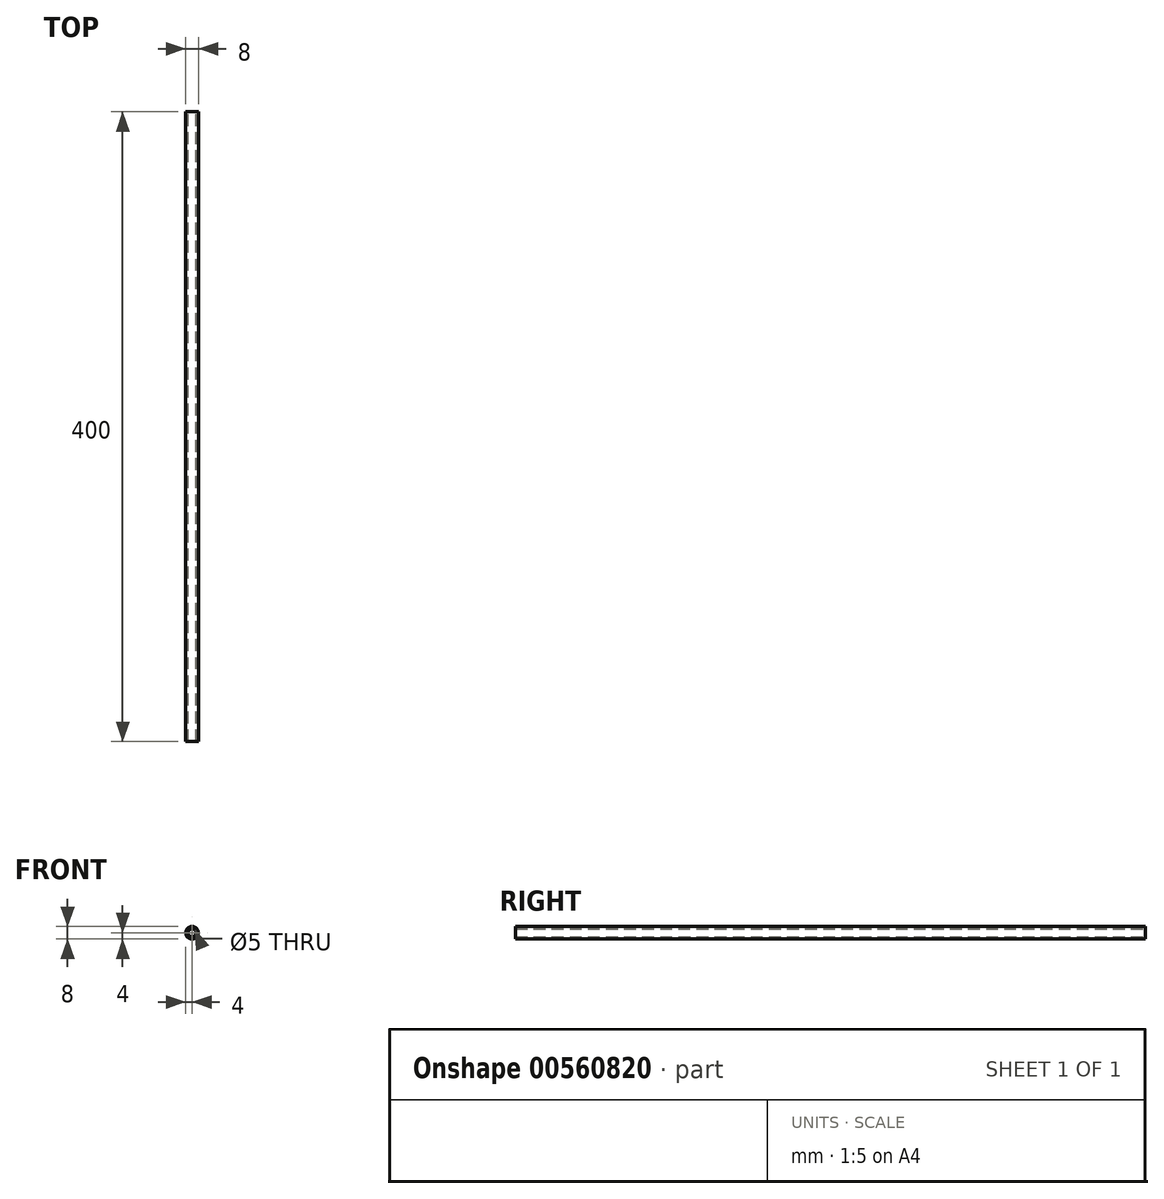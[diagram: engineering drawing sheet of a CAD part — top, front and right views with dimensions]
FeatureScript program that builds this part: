
annotation { "Feature Type Name" : "Feature", "Feature Type Description" : "" }
export const myFeature = defineFeature(function(context is Context, id is Id, definition is map)
    precondition{}
    {
        {
            var Q0;
            Q0=qCreatedBy(makeId("Front.planeOp"),FACE);
            var sketch = newSketch(context, id + "F0", { "sketchPlane" : qUnion([Q0])});
            skCircle(sketch, "E0", {"center": v(0, 0) * mm, "radius": 4 * mm});
            skCircle(sketch, "E1", {"center": v(0, 0) * mm, "radius": 2.5 * mm});
            skSolve(sketch);
        }
        {
            var Q0;
            Q0 = qSketchRegion(id + "F0", true);
            extrude(context, id + "F1", {"entities" : qUnion([Q0]), "endBound" : BoundingType.SYMMETRIC, "depth" : 400 * mm, "offsetDistance" : 25 * mm});
        }
    });
